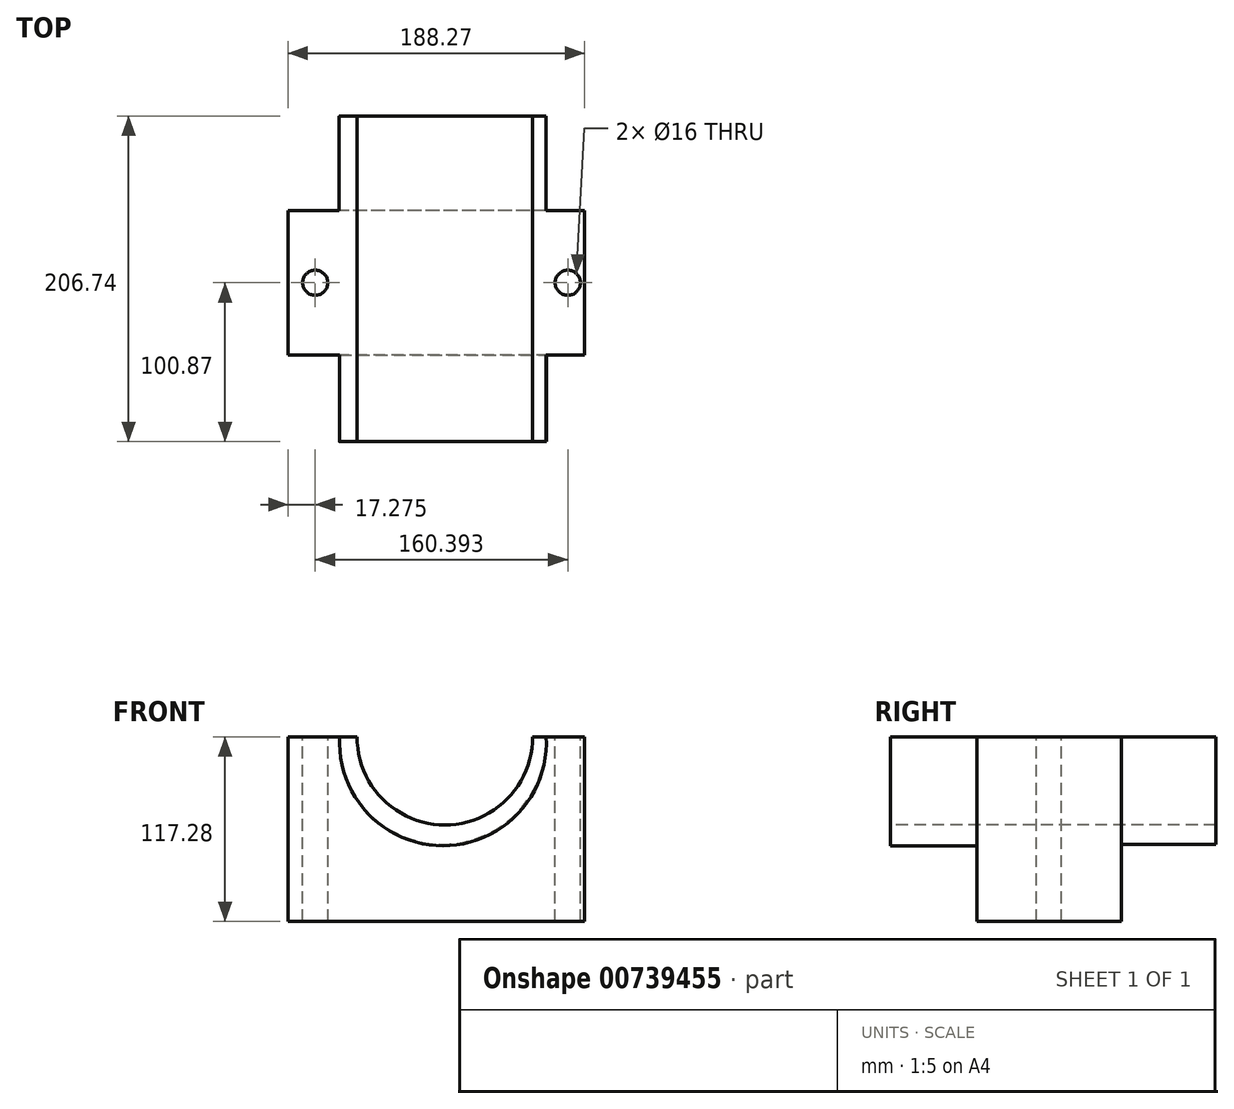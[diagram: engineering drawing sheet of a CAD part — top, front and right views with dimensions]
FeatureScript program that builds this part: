
annotation { "Feature Type Name" : "Feature", "Feature Type Description" : "" }
export const myFeature = defineFeature(function(context is Context, id is Id, definition is map)
    precondition{}
    {
        {
            var Q0;
            Q0=qCreatedBy(makeId("Top.planeOp"),FACE);
            var sketch = newSketch(context, id + "F0", { "sketchPlane" : qUnion([Q0])});
            skLineSegment(sketch, "E0.bottom", {"start": v(73.24, 45.87) * mm, "end": v(-73.24, 45.87) * mm});
            skLineSegment(sketch, "E0.top", {"start": v(73.24, -45.87) * mm, "end": v(-73.24, -45.87) * mm});
            skLineSegment(sketch, "E0.left", {"start": v(73.24, 45.87) * mm, "end": v(73.24, -45.87) * mm});
            skLineSegment(sketch, "E0.right", {"start": v(-73.24, 45.87) * mm, "end": v(-73.24, -45.87) * mm});
            skPoint(sketch, "E0.middle", {"position": v(0, 0) * mm});
            skSolve(sketch);
        }
        {
            var Q0;
            Q0=makeQuery(id+"F0.imprint","IMPRINT",FACE,{"disambiguationData":[TD([[makeQuery(id+"F0.imprint","IMPRINT",EDGE,{"derivedFrom":sQuery(id+"F0.wireOp",EDGE,"E0.bottom")}),1.0]])]});
            extrude(context, id + "F1", {"entities" : qUnion([Q0]), "depth" : 60.75 * mm, "offsetDistance" : 25 * mm});
        }
        {
            var Q0;
            Q0=makeQuery(id+"F1.opExtrude","CAP_FACE",FACE,{"disambiguationData":[OSD([sQuery(id+"F0.wireOp",EDGE,"E0.bottom"),sQuery(id+"F0.wireOp",EDGE,"E0.top"),sQuery(id+"F0.wireOp",EDGE,"E0.left"),sQuery(id+"F0.wireOp",EDGE,"E0.right")])],"isStart":false});
            extrude(context, id + "F2", {"entities" : qUnion([Q0]), "operationType" : NewBodyOperationType.ADD, "depth" : 56.53 * mm, "offsetDistance" : 25 * mm});
        }
        {
            var Q0;
            {var subQ0=sQuery(id+"F0.wireOp",EDGE,"E0.left");Q0=makeQuery(id+"F2.boolean.opBoolean","MERGE",FACE,{"derivedFrom":[makeQuery(id+"F1.opExtrude","SWEPT_FACE",FACE,{"disambiguationData":[OSD([subQ0])]}),makeQuery(id+"F2.opExtrude","SWEPT_FACE",FACE,{"disambiguationData":[OSD([subQ0])]})]});}
            extrude(context, id + "F3", {"entities" : qUnion([Q0]), "operationType" : NewBodyOperationType.ADD, "depth" : 41.78 * mm, "offsetDistance" : 25 * mm});
        }
        {
            var Q0;
            {var subQ0=sQuery(id+"F0.wireOp",EDGE,"E0.top");Q0=makeQuery(id+"F3.boolean.opBoolean","MERGE",FACE,{"derivedFrom":[makeQuery(id+"F2.boolean.opBoolean","MERGE",FACE,{"derivedFrom":[makeQuery(id+"F1.opExtrude","SWEPT_FACE",FACE,{"disambiguationData":[OSD([subQ0])]}),makeQuery(id+"F2.opExtrude","SWEPT_FACE",FACE,{"disambiguationData":[OSD([subQ0])]})]}),makeQuery(id+"F3.opExtrude","SWEPT_FACE",FACE,{"disambiguationData":[OSD([subQ0,sQuery(id+"F0.wireOp",EDGE,"E0.left")])]})]});}
            var sketch = newSketch(context, id + "F4", { "sketchPlane" : qUnion([Q0])});
            skArc(sketch, "E1", {"start": v(-29.38, 117.28) * mm, "mid": v(26.38, 61.26) * mm, "end": v(82.14, 117.28) * mm});
            skSolve(sketch);
        }
        {
            var Q0;
            {var subQ0=sQuery(id+"F4.wireOp",EDGE,"E1");Q0=makeQuery(id+"F4.imprint","IMPRINT",FACE,{"disambiguationData":[TD([[makeQuery(id+"F4.imprint","IMPRINT",EDGE,{"derivedFrom":subQ0}),1.0]])]});}
            extrude(context, id + "F5", {"entities" : qUnion([Q0]), "operationType" : NewBodyOperationType.REMOVE, "oppositeDirection" : true, "depth" : 104.85 * mm, "offsetDistance" : 25 * mm});
        }
        {
            var Q0;
            {var subQ0=sQuery(id+"F0.wireOp",EDGE,"E0.top");Q0=makeQuery(id+"F3.boolean.opBoolean","MERGE",FACE,{"derivedFrom":[makeQuery(id+"F2.boolean.opBoolean","MERGE",FACE,{"derivedFrom":[makeQuery(id+"F1.opExtrude","SWEPT_FACE",FACE,{"disambiguationData":[OSD([subQ0])]}),makeQuery(id+"F2.opExtrude","SWEPT_FACE",FACE,{"disambiguationData":[OSD([subQ0])]})]}),makeQuery(id+"F3.opExtrude","SWEPT_FACE",FACE,{"disambiguationData":[OSD([subQ0,sQuery(id+"F0.wireOp",EDGE,"E0.left")])]})]});}
            var sketch = newSketch(context, id + "F6", { "sketchPlane" : qUnion([Q0])});
            skArc(sketch, "E2", {"start": v(-40.44, 117.28) * mm, "mid": v(25.16, 48.03) * mm, "end": v(90.76, 117.28) * mm});
            skSolve(sketch);
        }
        {
            var Q0;
            {var subQ0=sQuery(id+"F6.wireOp",EDGE,"E2");Q0=makeQuery(id+"F6.imprint","IMPRINT",FACE,{"disambiguationData":[TD([[makeQuery(id+"F6.imprint","IMPRINT",EDGE,{"derivedFrom":subQ0}),1.0]])]});}
            extrude(context, id + "F7", {"entities" : qUnion([Q0]), "operationType" : NewBodyOperationType.ADD, "depth" : 30 * mm, "offsetDistance" : 25 * mm, "hasSecondDirection" : true, "secondDirectionOppositeDirection" : true, "secondDirectionDepth" : 41.72 * mm});
        }
        {
            var Q0;
            Q0=makeQuery(id+"F7.opExtrude","CAP_FACE",FACE,{"disambiguationData":[OSD([sQuery(id+"F0.wireOp",EDGE,"E0.top"),sQuery(id+"F0.wireOp",EDGE,"E0.left"),sQuery(id+"F4.wireOp",EDGE,"E1"),sQuery(id+"F6.wireOp",EDGE,"E2")])],"isStart":false});
            var sketch = newSketch(context, id + "F8", { "sketchPlane" : qUnion([Q0])});
            skSolve(sketch);
        }
        {
            var Q0;
            {var subQ0=sQuery(id+"F6.wireOp",EDGE,"E2");Q0=makeQuery(id+"F8.imprint","IMPRINT",FACE,{"disambiguationData":[TD([[makeQuery(id+"F8.imprint","IMPRINT",EDGE,{"derivedFrom":makeQuery(id+"F7.opExtrude","CAP_EDGE",EDGE,{"disambiguationData":[OSD([subQ0])],"isStart":false})}),1.0]])]});}
            extrude(context, id + "F9", {"entities" : qUnion([Q0]), "operationType" : NewBodyOperationType.ADD, "depth" : 25 * mm, "offsetDistance" : 25 * mm, "hasSecondDirection" : true, "secondDirectionOppositeDirection" : true, "secondDirectionDepth" : 25 * mm});
        }
        {
            var Q0;
            {var subQ0=sQuery(id+"F0.wireOp",EDGE,"E0.left");var subQ1=makeQuery(id+"F3.opExtrude","SWEPT_FACE",FACE,{"disambiguationData":[OSD([subQ0]),TDD([makeQuery(id+"F2.opExtrude","CAP_EDGE",EDGE,{"disambiguationData":[OSD([subQ0])],"isStart":false})])]});var subQ2=sQuery(id+"F0.wireOp",EDGE,"E0.top");var subQ3=sQuery(id+"F0.wireOp",EDGE,"E0.bottom");var subQ4=makeQuery(id+"F2.opExtrude","CAP_FACE",FACE,{"disambiguationData":[OSD([subQ3,subQ2,subQ0,sQuery(id+"F0.wireOp",EDGE,"E0.right")])],"isStart":false});var subQ8=makeQuery(id+"F3.opExtrude","CAP_FACE",FACE,{"disambiguationData":[OSD([subQ0])],"isStart":false});var subQ9=sQuery(id+"F4.wireOp",EDGE,"E1");var subQ11=makeQuery(id+"F5.boolean.opBoolean","SPLIT",EDGE,{"disambiguationData":[TD([subQ8])],"derivedFrom":makeQuery(id+"F3.boolean.opBoolean","MERGE",EDGE,{"derivedFrom":[makeQuery(id+"F2.opExtrude","CAP_EDGE",EDGE,{"disambiguationData":[OSD([subQ2])],"isStart":false}),makeQuery(id+"F3.opExtrude","SWEPT_EDGE",EDGE,{"disambiguationData":[OSD([subQ2,subQ0]),TDD([makeQuery(id+"F2.opExtrude","CAP_VERTEX",VERTEX,{"disambiguationData":[OSD([subQ2,subQ0])],"isStart":false})])]})]})});var subQ12=makeQuery(id+"F6.imprint","IMPRINT",EDGE,{"disambiguationData":[TD([[makeQuery(id+"F6.imprint","INTERSECT",VERTEX,{"derivedFrom":[makeQuery(id+"F5.boolean.opBoolean","COPY",EDGE,{"derivedFrom":makeQuery(id+"F5.opExtrude","CAP_EDGE",EDGE,{"disambiguationData":[OSD([subQ9])],"isStart":true})}),subQ11]}),1.0]])],"derivedFrom":subQ11});Q0=makeQuery(id+"F9.boolean.opBoolean","MERGE",FACE,{"derivedFrom":[makeQuery(id+"F7.boolean.opBoolean","MERGE",FACE,{"derivedFrom":[makeQuery(id+"F5.boolean.opBoolean","SPLIT",FACE,{"disambiguationData":[TD([subQ8])],"derivedFrom":makeQuery(id+"F3.boolean.opBoolean","MERGE",FACE,{"derivedFrom":[subQ4,subQ1]})}),makeQuery(id+"F7.opExtrude","SWEPT_FACE",FACE,{"disambiguationData":[OSD([subQ2,subQ0]),TDD([subQ12])]})]}),makeQuery(id+"F9.opExtrude","SWEPT_FACE",FACE,{"disambiguationData":[OSD([subQ2,subQ0]),TDD([makeQuery(id+"F8.imprint","IMPRINT",EDGE,{"derivedFrom":makeQuery(id+"F7.opExtrude","CAP_EDGE",EDGE,{"disambiguationData":[OSD([subQ2,subQ0]),TDD([subQ12])],"isStart":false})})])]})]});}
            var sketch = newSketch(context, id + "F10", { "sketchPlane" : qUnion([Q0])});
            skLineSegment(sketch, "E3", {"start": v(90.76, -45.87) * mm, "end": v(90.76, 45.87) * mm});
            skSolve(sketch);
        }
        {
            var Q0;
            {var subQ0=sQuery(id+"F0.wireOp",EDGE,"E0.right");var subQ2=sQuery(id+"F0.wireOp",EDGE,"E0.top");var subQ4=makeQuery(id+"F1.opExtrude","SWEPT_FACE",FACE,{"disambiguationData":[OSD([subQ0])]});var subQ6=sQuery(id+"F0.wireOp",EDGE,"E0.left");var subQ7=sQuery(id+"F0.wireOp",EDGE,"E0.bottom");var subQ8=makeQuery(id+"F2.opExtrude","CAP_FACE",FACE,{"disambiguationData":[OSD([subQ7,subQ2,subQ6,subQ0])],"isStart":false});var subQ9=makeQuery(id+"F3.opExtrude","SWEPT_FACE",FACE,{"disambiguationData":[OSD([subQ6]),TDD([makeQuery(id+"F2.opExtrude","CAP_EDGE",EDGE,{"disambiguationData":[OSD([subQ6])],"isStart":false})])]});var subQ11=sQuery(id+"F4.wireOp",EDGE,"E1");var subQ13=makeQuery(id+"F5.boolean.opBoolean","SPLIT",EDGE,{"disambiguationData":[TD([subQ4])],"derivedFrom":makeQuery(id+"F3.boolean.opBoolean","MERGE",EDGE,{"derivedFrom":[makeQuery(id+"F2.opExtrude","CAP_EDGE",EDGE,{"disambiguationData":[OSD([subQ2])],"isStart":false}),makeQuery(id+"F3.opExtrude","SWEPT_EDGE",EDGE,{"disambiguationData":[OSD([subQ2,subQ6]),TDD([makeQuery(id+"F2.opExtrude","CAP_VERTEX",VERTEX,{"disambiguationData":[OSD([subQ2,subQ6])],"isStart":false})])]})]})});var subQ14=makeQuery(id+"F6.imprint","IMPRINT",EDGE,{"disambiguationData":[TD([[makeQuery(id+"F6.imprint","INTERSECT",VERTEX,{"derivedFrom":[makeQuery(id+"F5.boolean.opBoolean","COPY",EDGE,{"derivedFrom":makeQuery(id+"F5.opExtrude","CAP_EDGE",EDGE,{"disambiguationData":[OSD([subQ11])],"isStart":true})}),subQ13]}),-1.0]])],"derivedFrom":subQ13});Q0=makeQuery(id+"F9.boolean.opBoolean","MERGE",FACE,{"derivedFrom":[makeQuery(id+"F7.boolean.opBoolean","MERGE",FACE,{"derivedFrom":[makeQuery(id+"F5.boolean.opBoolean","SPLIT",FACE,{"disambiguationData":[TD([subQ4])],"derivedFrom":makeQuery(id+"F3.boolean.opBoolean","MERGE",FACE,{"derivedFrom":[subQ8,subQ9]})}),makeQuery(id+"F7.opExtrude","SWEPT_FACE",FACE,{"disambiguationData":[OSD([subQ2,subQ6]),TDD([subQ14])]})]}),makeQuery(id+"F9.opExtrude","SWEPT_FACE",FACE,{"disambiguationData":[OSD([subQ2,subQ6]),TDD([makeQuery(id+"F8.imprint","IMPRINT",EDGE,{"derivedFrom":makeQuery(id+"F7.opExtrude","CAP_EDGE",EDGE,{"disambiguationData":[OSD([subQ2,subQ6]),TDD([subQ14])],"isStart":false})})])]})]});}
            var sketch = newSketch(context, id + "F11", { "sketchPlane" : qUnion([Q0])});
            skLineSegment(sketch, "E4", {"start": v(-40.44, -45.87) * mm, "end": v(-40.44, 45.87) * mm});
            skPoint(sketch, "E4.endSnap0", {"position": v(-51.31, 45.87) * mm});
            skSolve(sketch);
        }
        {
            var Q0;
            {var subQ0=sQuery(id+"F0.wireOp",EDGE,"E0.bottom");Q0=makeQuery(id+"F3.boolean.opBoolean","MERGE",FACE,{"derivedFrom":[makeQuery(id+"F2.boolean.opBoolean","MERGE",FACE,{"derivedFrom":[makeQuery(id+"F1.opExtrude","SWEPT_FACE",FACE,{"disambiguationData":[OSD([subQ0])]}),makeQuery(id+"F2.opExtrude","SWEPT_FACE",FACE,{"disambiguationData":[OSD([subQ0])]})]}),makeQuery(id+"F3.opExtrude","SWEPT_FACE",FACE,{"disambiguationData":[OSD([subQ0,sQuery(id+"F0.wireOp",EDGE,"E0.left")])]})]});}
            var sketch = newSketch(context, id + "F12", { "sketchPlane" : qUnion([Q0])});
            skArc(sketch, "E5", {"start": v(-90.59, 117.28) * mm, "mid": v(-24.94, 49.01) * mm, "end": v(40.72, 117.28) * mm});
            skSolve(sketch);
        }
        {
            var Q0;
            {var subQ0=sQuery(id+"F12.wireOp",EDGE,"E5");Q0=makeQuery(id+"F12.imprint","IMPRINT",FACE,{"disambiguationData":[TD([[makeQuery(id+"F12.imprint","IMPRINT",EDGE,{"derivedFrom":subQ0}),1.0]])]});}
            extrude(context, id + "F13", {"entities" : qUnion([Q0]), "operationType" : NewBodyOperationType.ADD, "depth" : 30 * mm, "offsetDistance" : 25 * mm});
        }
        {
            var Q0;
            Q0=makeQuery(id+"F13.opExtrude","CAP_FACE",FACE,{"disambiguationData":[OSD([sQuery(id+"F0.wireOp",EDGE,"E0.bottom"),sQuery(id+"F0.wireOp",EDGE,"E0.left"),sQuery(id+"F4.wireOp",EDGE,"E1"),sQuery(id+"F12.wireOp",EDGE,"E5")])],"isStart":false});
            extrude(context, id + "F14", {"entities" : qUnion([Q0]), "operationType" : NewBodyOperationType.ADD, "depth" : 30 * mm, "offsetDistance" : 25 * mm});
        }
        {
            var Q0;
            {var subQ0=sQuery(id+"F10.wireOp",EDGE,"E3");Q0=makeQuery(id+"F10.imprint","IMPRINT",FACE,{"disambiguationData":[TD([[makeQuery(id+"F10.imprint","IMPRINT",EDGE,{"derivedFrom":subQ0}),-1.0]])]});}
            var sketch = newSketch(context, id + "F15", { "sketchPlane" : qUnion([Q0])});
            skPoint(sketch, "E6", {"position": v(104.43, 0) * mm});
            skPoint(sketch, "E7", {"position": v(-55.87, 0) * mm});
            skSolve(sketch);
        }
        {
            var Q0;
            Q0=sQuery(id+"F15.wireOp",VERTEX,"E6");
            var Q1;
            Q1=makeQuery(id+"F1.opExtrude","SWEPT_BODY",BODY,{"disambiguationData":[OSD([sQuery(id+"F0.wireOp",EDGE,"E0.bottom"),sQuery(id+"F0.wireOp",EDGE,"E0.top"),sQuery(id+"F0.wireOp",EDGE,"E0.left"),sQuery(id+"F0.wireOp",EDGE,"E0.right")])]});
            hole(context, id + "F16", {"style" : HoleStyle.SIMPLE, "endStyle" : HoleEndStyle.THROUGH, "holeDiameter" : 16 * mm, "majorDiameter" : 5 * mm, "isTappedThrough" : true, "tappedDepth" : 12 * mm, "tapClearance" : 3, "locations" : qUnion([Q0]), "scope" : qUnion([Q1])});
        }
        {
            var Q0;
            {var subQ0=sQuery(id+"F11.wireOp",EDGE,"E4");Q0=makeQuery(id+"F11.imprint","IMPRINT",FACE,{"disambiguationData":[TD([[makeQuery(id+"F11.imprint","IMPRINT",EDGE,{"derivedFrom":subQ0}),1.0]])]});}
            var sketch = newSketch(context, id + "F17", { "sketchPlane" : qUnion([Q0])});
            skPoint(sketch, "E8", {"position": v(-55.96, 0) * mm});
            skSolve(sketch);
        }
        {
            var Q0;
            Q0=sQuery(id+"F17.wireOp",VERTEX,"E8");
            var Q1;
            Q1=makeQuery(id+"F1.opExtrude","SWEPT_BODY",BODY,{"disambiguationData":[OSD([sQuery(id+"F0.wireOp",EDGE,"E0.bottom"),sQuery(id+"F0.wireOp",EDGE,"E0.top"),sQuery(id+"F0.wireOp",EDGE,"E0.left"),sQuery(id+"F0.wireOp",EDGE,"E0.right")])]});
            hole(context, id + "F18", {"style" : HoleStyle.SIMPLE, "endStyle" : HoleEndStyle.THROUGH, "holeDiameter" : 16 * mm, "majorDiameter" : 5 * mm, "isTappedThrough" : true, "tappedDepth" : 12 * mm, "tapClearance" : 3, "locations" : qUnion([Q0]), "scope" : qUnion([Q1])});
        }
    });
